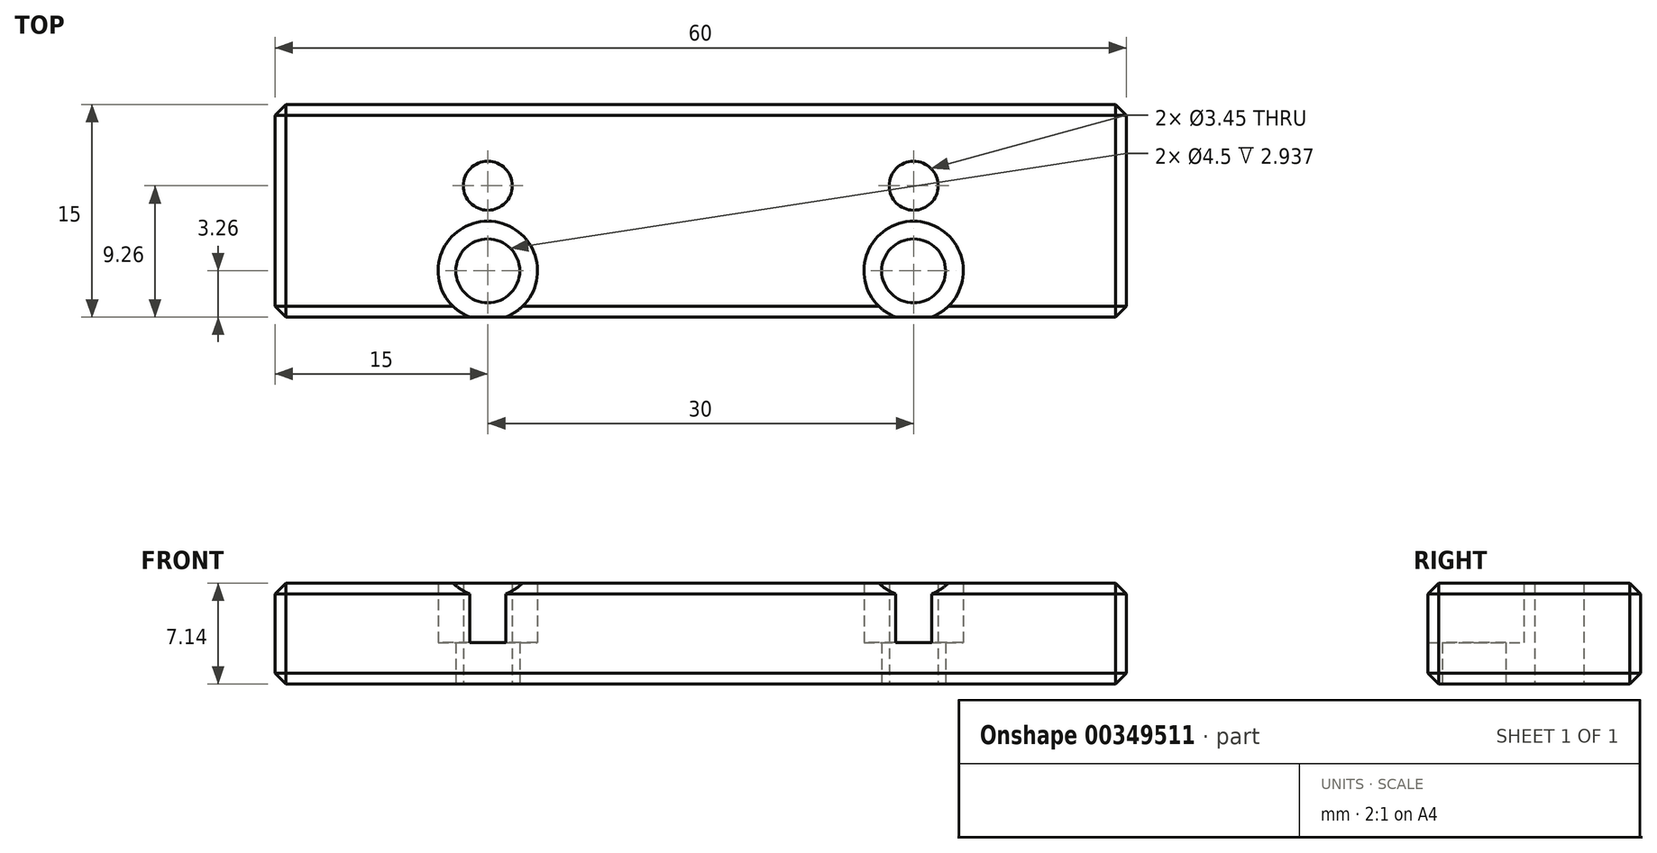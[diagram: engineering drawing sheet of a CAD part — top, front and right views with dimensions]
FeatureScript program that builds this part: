
annotation { "Feature Type Name" : "Feature", "Feature Type Description" : "" }
export const myFeature = defineFeature(function(context is Context, id is Id, definition is map)
    precondition{}
    {
        {
            var Q0;
            Q0=qCreatedBy(makeId("Top.planeOp"),FACE);
            var sketch = newSketch(context, id + "F0", { "sketchPlane" : qUnion([Q0])});
            skLineSegment(sketch, "E0.bottom", {"start": v(30, -7.5) * mm, "end": v(-30, -7.5) * mm});
            skLineSegment(sketch, "E0.top", {"start": v(30, 7.5) * mm, "end": v(-30, 7.5) * mm});
            skLineSegment(sketch, "E0.left", {"start": v(30, -7.5) * mm, "end": v(30, 7.5) * mm});
            skLineSegment(sketch, "E0.right", {"start": v(-30, -7.5) * mm, "end": v(-30, 7.5) * mm});
            skPoint(sketch, "E0.middle", {"position": v(0, 0) * mm});
            skSolve(sketch);
        }
        {
            var Q0;
            Q0 = qSketchRegion(id + "F0", true);
            extrude(context, id + "F1", {"entities" : qUnion([Q0]), "depth" : 7.14 * mm});
        }
        {
            var Q0;
            Q0=makeQuery(id+"F1.opExtrude","CAP_FACE",FACE,{"disambiguationData":[OSD([sQuery(id+"F0.wireOp",EDGE,"E0.bottom"),sQuery(id+"F0.wireOp",EDGE,"E0.top"),sQuery(id+"F0.wireOp",EDGE,"E0.left"),sQuery(id+"F0.wireOp",EDGE,"E0.right")])],"isStart":false});
            var sketch = newSketch(context, id + "F2", { "sketchPlane" : qUnion([Q0])});
            skPoint(sketch, "E1", {"position": v(15, 1.76) * mm});
            skPoint(sketch, "E2", {"position": v(-15, 1.76) * mm});
            skLineSegment(sketch, "E3", {"start": v(0, -7.5) * mm, "end": v(0, 7.5) * mm, "construction": true});
            skLineSegment(sketch, "E4", {"start": v(-30, 0) * mm, "end": v(30, 0) * mm, "construction": true});
            skPoint(sketch, "E5", {"position": v(-15, -4.24) * mm});
            skPoint(sketch, "E6", {"position": v(15, -4.24) * mm});
            skSolve(sketch);
        }
        {
            var Q0;
            Q0=sQuery(id+"F2.wireOp",VERTEX,"E2");
            var Q1;
            Q1=sQuery(id+"F2.wireOp",VERTEX,"E1");
            var Q2;
            Q2=makeQuery(id+"F1.opExtrude","SWEPT_BODY",BODY,{"disambiguationData":[OSD([sQuery(id+"F0.wireOp",EDGE,"E0.bottom"),sQuery(id+"F0.wireOp",EDGE,"E0.top"),sQuery(id+"F0.wireOp",EDGE,"E0.left"),sQuery(id+"F0.wireOp",EDGE,"E0.right")])]});
            hole(context, id + "F3", {"style" : HoleStyle.SIMPLE, "endStyle" : HoleEndStyle.THROUGH, "holeDiameter" : 3.45 * mm, "isTappedThrough" : true, "tappedDepth" : 12.7 * mm, "tapClearance" : 3, "locations" : qUnion([Q0, Q1]), "scope" : qUnion([Q2])});
        }
        {
            var Q0;
            Q0=sQuery(id+"F2.wireOp",VERTEX,"E5");
            var Q1;
            Q1=sQuery(id+"F2.wireOp",VERTEX,"E6");
            var Q2;
            Q2=makeQuery(id+"F1.opExtrude","SWEPT_BODY",BODY,{"disambiguationData":[OSD([sQuery(id+"F0.wireOp",EDGE,"E0.bottom"),sQuery(id+"F0.wireOp",EDGE,"E0.top"),sQuery(id+"F0.wireOp",EDGE,"E0.left"),sQuery(id+"F0.wireOp",EDGE,"E0.right")])]});
            hole(context, id + "F4", {"style" : HoleStyle.C_BORE, "endStyle" : HoleEndStyle.THROUGH, "holeDiameter" : 4.5 * mm, "cBoreDiameter" : 7 * mm, "cBoreDepth" : 4.2 * mm, "isTappedThrough" : true, "tappedDepth" : 12.7 * mm, "tapClearance" : 3, "locations" : qUnion([Q0, Q1]), "scope" : qUnion([Q2])});
        }
        {
            var Q0;
            Q0=makeQuery(id+"F1.opExtrude","CAP_EDGE",EDGE,{"disambiguationData":[OSD([sQuery(id+"F0.wireOp",EDGE,"E0.bottom")])],"isStart":false});
            var Q1;
            Q1=makeQuery(id+"F1.opExtrude","CAP_EDGE",EDGE,{"disambiguationData":[OSD([sQuery(id+"F0.wireOp",EDGE,"E0.right")])],"isStart":false});
            var Q2;
            Q2=makeQuery(id+"F1.opExtrude","CAP_EDGE",EDGE,{"disambiguationData":[OSD([sQuery(id+"F0.wireOp",EDGE,"E0.top")])],"isStart":false});
            var Q3;
            Q3=makeQuery(id+"F1.opExtrude","CAP_EDGE",EDGE,{"disambiguationData":[OSD([sQuery(id+"F0.wireOp",EDGE,"E0.left")])],"isStart":false});
            var Q4;
            Q4=makeQuery(id+"F1.opExtrude","SWEPT_EDGE",EDGE,{"disambiguationData":[OSD([sQuery(id+"F0.wireOp",EDGE,"E0.bottom"),sQuery(id+"F0.wireOp",EDGE,"E0.left")])]});
            var Q5;
            Q5=makeQuery(id+"F1.opExtrude","SWEPT_EDGE",EDGE,{"disambiguationData":[OSD([sQuery(id+"F0.wireOp",EDGE,"E0.top"),sQuery(id+"F0.wireOp",EDGE,"E0.left")])]});
            var Q6;
            Q6=makeQuery(id+"F1.opExtrude","CAP_EDGE",EDGE,{"disambiguationData":[OSD([sQuery(id+"F0.wireOp",EDGE,"E0.left")])],"isStart":true});
            var Q7;
            Q7=makeQuery(id+"F1.opExtrude","CAP_EDGE",EDGE,{"disambiguationData":[OSD([sQuery(id+"F0.wireOp",EDGE,"E0.top")])],"isStart":true});
            var Q8;
            Q8=makeQuery(id+"F1.opExtrude","SWEPT_FACE",FACE,{"disambiguationData":[OSD([sQuery(id+"F0.wireOp",EDGE,"E0.top")])]});
            var Q9;
            Q9=makeQuery(id+"F1.opExtrude","CAP_EDGE",EDGE,{"disambiguationData":[OSD([sQuery(id+"F0.wireOp",EDGE,"E0.bottom")])],"isStart":true});
            var Q10;
            Q10=makeQuery(id+"F1.opExtrude","SWEPT_EDGE",EDGE,{"disambiguationData":[OSD([sQuery(id+"F0.wireOp",EDGE,"E0.bottom"),sQuery(id+"F0.wireOp",EDGE,"E0.right")])]});
            var Q11;
            Q11=makeQuery(id+"F1.opExtrude","CAP_EDGE",EDGE,{"disambiguationData":[OSD([sQuery(id+"F0.wireOp",EDGE,"E0.right")])],"isStart":true});
            chamfer(context, id + "F5", {"entities" : qUnion([Q0, Q1, Q2, Q3, Q4, Q5, Q6, Q7, Q8, Q9, Q10, Q11]), "width" : 0.76 * mm, "tangentPropagation" : true});
        }
    });
